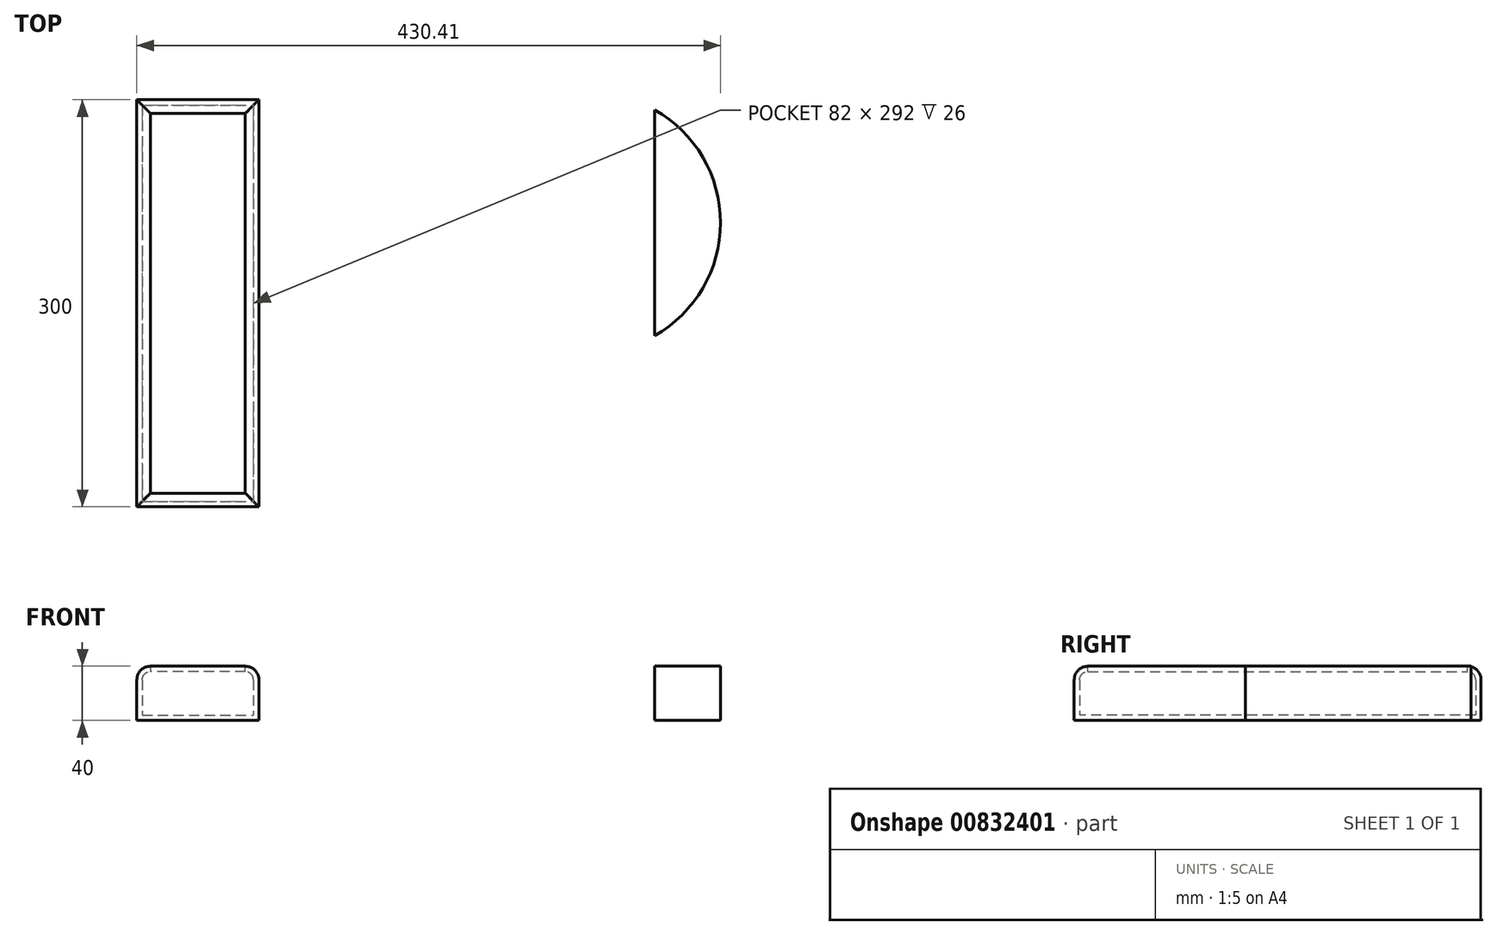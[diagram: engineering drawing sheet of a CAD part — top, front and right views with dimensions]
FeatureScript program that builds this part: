
annotation { "Feature Type Name" : "Feature", "Feature Type Description" : "" }
export const myFeature = defineFeature(function(context is Context, id is Id, definition is map)
    precondition{}
    {
        {
            var Q0;
            Q0=qCreatedBy(makeId("Top.planeOp"),FACE);
            var sketch = newSketch(context, id + "F0", { "sketchPlane" : qUnion([Q0])});
            skLineSegment(sketch, "E0.bottom", {"start": v(-180.06, 52.57) * mm, "end": v(-90.06, 52.57) * mm});
            skLineSegment(sketch, "E0.top", {"start": v(-180.06, -247.43) * mm, "end": v(-90.06, -247.43) * mm});
            skLineSegment(sketch, "E0.left", {"start": v(-180.06, 52.57) * mm, "end": v(-180.06, -247.43) * mm});
            skLineSegment(sketch, "E0.right", {"start": v(-90.06, 52.57) * mm, "end": v(-90.06, -247.43) * mm});
            skPoint(sketch, "E0.middle", {"position": v(-135.06, -97.43) * mm});
            skSolve(sketch);
        }
        {
            var Q0;
            Q0 = qSketchRegion(id + "F0", true);
            extrude(context, id + "F1", {"entities" : qUnion([Q0]), "depth" : 40 * mm, "offsetDistance" : 25 * mm});
        }
        {
            var Q0;
            Q0=makeQuery(id+"F1.opExtrude","CAP_EDGE",EDGE,{"disambiguationData":[OSD([sQuery(id+"F0.wireOp",EDGE,"E0.right")])],"isStart":false});
            var Q1;
            Q1=makeQuery(id+"F1.opExtrude","CAP_EDGE",EDGE,{"disambiguationData":[OSD([sQuery(id+"F0.wireOp",EDGE,"E0.top")])],"isStart":false});
            var Q2;
            Q2=makeQuery(id+"F1.opExtrude","CAP_EDGE",EDGE,{"disambiguationData":[OSD([sQuery(id+"F0.wireOp",EDGE,"E0.left")])],"isStart":false});
            var Q3;
            Q3=makeQuery(id+"F1.opExtrude","CAP_EDGE",EDGE,{"disambiguationData":[OSD([sQuery(id+"F0.wireOp",EDGE,"E0.bottom")])],"isStart":false});
            fillet(context, id + "F2", {"entities" : qUnion([Q0, Q1, Q2, Q3]), "radius" : 10 * mm, "tangentPropagation" : true, "allowEdgeOverflow" : false});
        }
        {
            var Q0;
            Q0=makeQuery(id+"F1.opExtrude","CAP_FACE",FACE,{"disambiguationData":[OSD([sQuery(id+"F0.wireOp",EDGE,"E0.bottom"),sQuery(id+"F0.wireOp",EDGE,"E0.top"),sQuery(id+"F0.wireOp",EDGE,"E0.left"),sQuery(id+"F0.wireOp",EDGE,"E0.right")])],"isStart":false});
            shell(context, id + "F3", {"entities" : qUnion([Q0]), "thickness" : 4 * mm});
        }
        {
            var Q0;
            Q0=qCreatedBy(makeId("Top.planeOp"),FACE);
            var sketch = newSketch(context, id + "F4", { "sketchPlane" : qUnion([Q0])});
            skLineSegment(sketch, "E1", {"start": v(201.77, -121.3) * mm, "end": v(201.77, 45.15) * mm});
            skArc(sketch, "E2", {"start": v(201.77, -121.3) * mm, "mid": v(250.35, -38.07) * mm, "end": v(201.77, 45.15) * mm});
            skSolve(sketch);
        }
        {
            var Q0;
            Q0=makeQuery(id+"F4.imprint","IMPRINT",FACE,{"disambiguationData":[TD([[makeQuery(id+"F4.imprint","IMPRINT",EDGE,{"derivedFrom":sQuery(id+"F4.wireOp",EDGE,"E1")}),-1.0]])]});
            extrude(context, id + "F5", {"entities" : qUnion([Q0]), "depth" : 40 * mm, "offsetDistance" : 25 * mm});
        }
    });
